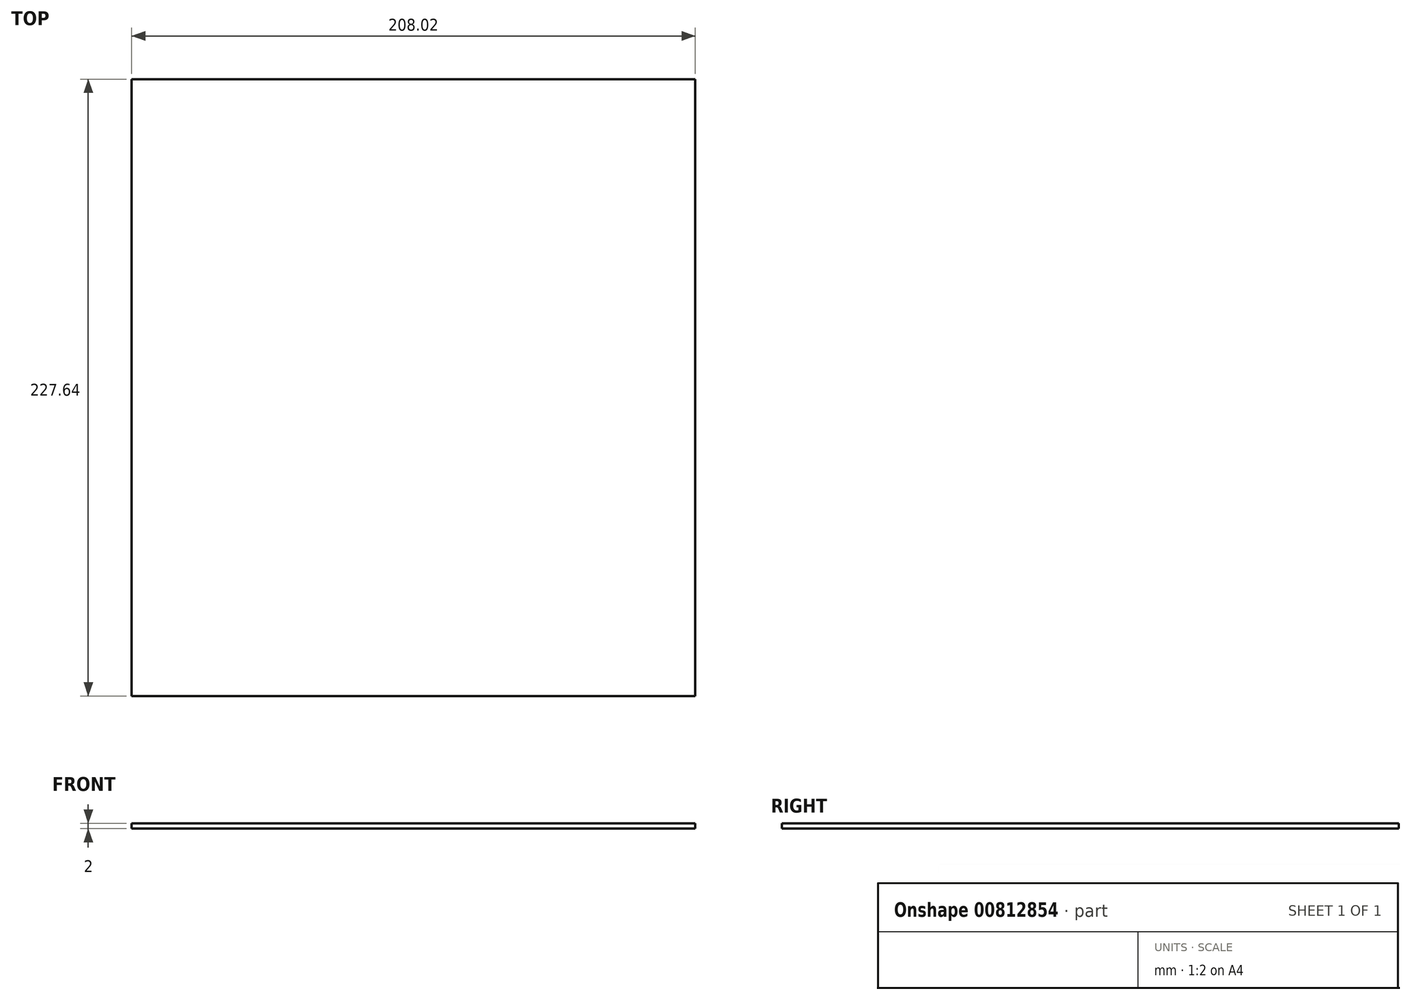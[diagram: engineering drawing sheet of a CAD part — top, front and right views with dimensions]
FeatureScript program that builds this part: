
annotation { "Feature Type Name" : "Feature", "Feature Type Description" : "" }
export const myFeature = defineFeature(function(context is Context, id is Id, definition is map)
    precondition{}
    {
        {
            var Q0;
            Q0=qCreatedBy(makeId("Top.planeOp"),FACE);
            var sketch = newSketch(context, id + "F0", { "sketchPlane" : qUnion([Q0])});
            skLineSegment(sketch, "E0.bottom", {"start": v(104, 113.82) * mm, "end": v(-104, 113.82) * mm});
            skLineSegment(sketch, "E0.top", {"start": v(104, -113.82) * mm, "end": v(-104, -113.82) * mm});
            skLineSegment(sketch, "E0.left", {"start": v(104, 113.82) * mm, "end": v(104, -113.82) * mm});
            skLineSegment(sketch, "E0.right", {"start": v(-104, 113.82) * mm, "end": v(-104, -113.82) * mm});
            skPoint(sketch, "E0.middle", {"position": v(0, 0) * mm});
            skSolve(sketch);
        }
        {
            var Q0;
            Q0 = qSketchRegion(id + "F0", true);
            extrude(context, id + "F1", {"entities" : qUnion([Q0]), "depth" : 2 * mm, "offsetDistance" : 25 * mm});
        }
    });
